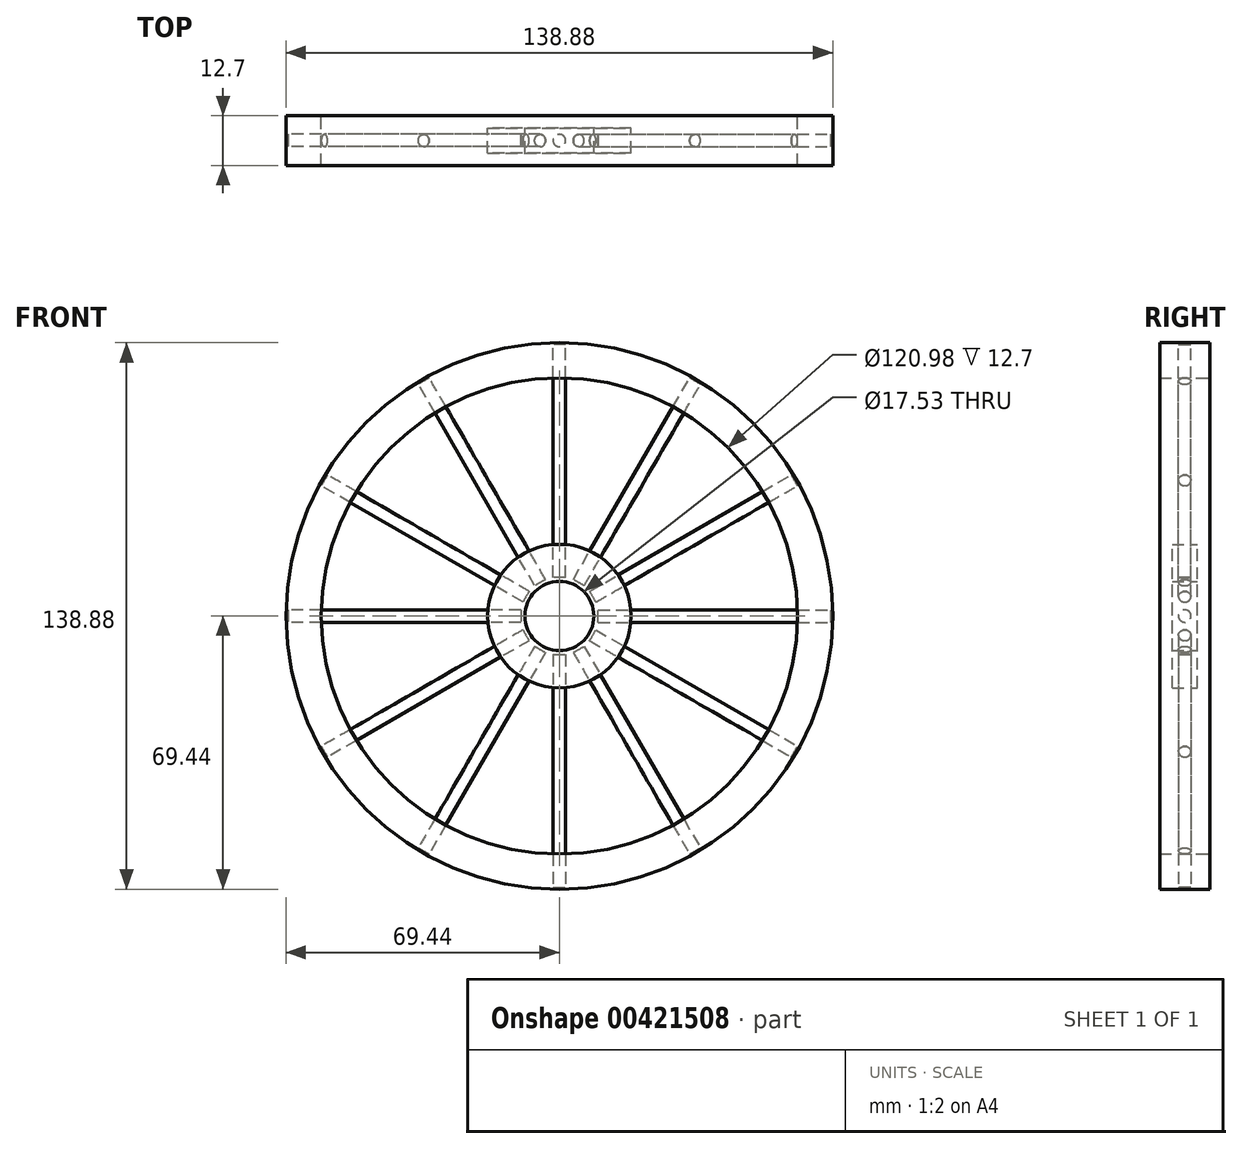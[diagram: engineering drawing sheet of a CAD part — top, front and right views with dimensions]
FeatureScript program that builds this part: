
annotation { "Feature Type Name" : "Feature", "Feature Type Description" : "" }
export const myFeature = defineFeature(function(context is Context, id is Id, definition is map)
    precondition{}
    {
        {
            var Q0;
            Q0=qCreatedBy(makeId("Front.planeOp"),FACE);
            var sketch = newSketch(context, id + "F0", { "sketchPlane" : qUnion([Q0])});
            skCircle(sketch, "E0", {"center": v(0, 0) * mm, "radius": 69.44 * mm});
            skCircle(sketch, "E1", {"center": v(0, 0) * mm, "radius": 60.5 * mm});
            skCircle(sketch, "E2", {"center": v(0, 0) * mm, "radius": 18.22 * mm});
            skCircle(sketch, "E3", {"center": v(0, 0) * mm, "radius": 8.76 * mm});
            skLineSegment(sketch, "E4", {"start": v(-8.76, 0) * mm, "end": v(0, 0) * mm});
            skLineSegment(sketch, "E5", {"start": v(8.76, 0) * mm, "end": v(0, 0) * mm});
            skLineSegment(sketch, "E6", {"start": v(0, 8.76) * mm, "end": v(0, 0) * mm});
            skLineSegment(sketch, "E7", {"start": v(0, 0) * mm, "end": v(0, -8.76) * mm});
            skPoint(sketch, "E8.start.orphan", {"position": v(-60.5, 0) * mm});
            skSolve(sketch);
        }
        {
            var Q0;
            Q0=makeQuery(id+"F0.imprint","IMPRINT",FACE,{"disambiguationData":[TD([[makeQuery(id+"F0.imprint","IMPRINT",EDGE,{"derivedFrom":sQuery(id+"F0.wireOp",EDGE,"E2")}),1.0]])]});
            extrude(context, id + "F1", {"entities" : qUnion([Q0]), "endBound" : BoundingType.SYMMETRIC, "depth" : 6.35 * mm});
        }
        {
            var Q0;
            Q0 = qSketchRegion(id + "F0", true);
            extrude(context, id + "F2", {"entities" : qUnion([Q0]), "endBound" : BoundingType.SYMMETRIC, "depth" : 12.7 * mm});
        }
        {
            var Q0;
            Q0=qCreatedBy(makeId("Right.planeOp"),FACE);
            cPlane(context, id + "F3", {"entities" : qUnion([Q0]), "cplaneType" : CPlaneType.OFFSET, "offset" : 68.94 * mm, "width" : 152.4 * mm, "height" : 152.4 * mm});
        }
        {
            var Q0;
            Q0=qCreatedBy(id+"F3.planeOp",FACE);
            var sketch = newSketch(context, id + "F4", { "sketchPlane" : qUnion([Q0])});
            skCircle(sketch, "E9", {"center": v(0, 0) * mm, "radius": 1.59 * mm});
            skSolve(sketch);
        }
        {
            var Q0;
            Q0=makeQuery(id+"F4.imprint","IMPRINT",FACE,{"disambiguationData":[TD([[makeQuery(id+"F4.imprint","IMPRINT",EDGE,{"derivedFrom":sQuery(id+"F4.wireOp",EDGE,"E9")}),1.0]])]});
            extrude(context, id + "F5", {"entities" : qUnion([Q0]), "oppositeDirection" : true, "depth" : 59.13 * mm});
        }
        {
            var Q0;
            Q0=makeQuery(id+"F5.opExtrude","SWEPT_BODY",BODY,{"disambiguationData":[OSD([sQuery(id+"F4.wireOp",EDGE,"E9")])]});
            var Q1;
            Q1=makeQuery(id+"F1.opExtrude","CAP_EDGE",EDGE,{"disambiguationData":[OSD([sQuery(id+"F0.wireOp",EDGE,"E2")])],"isStart":false});
            circularPattern(context, id + "F6", {"entities" : qUnion([Q0]), "axis" : qUnion([Q1]), "angle" : 360 * degree, "instanceCount" : 12, "equalSpace" : true});
        }
    });
